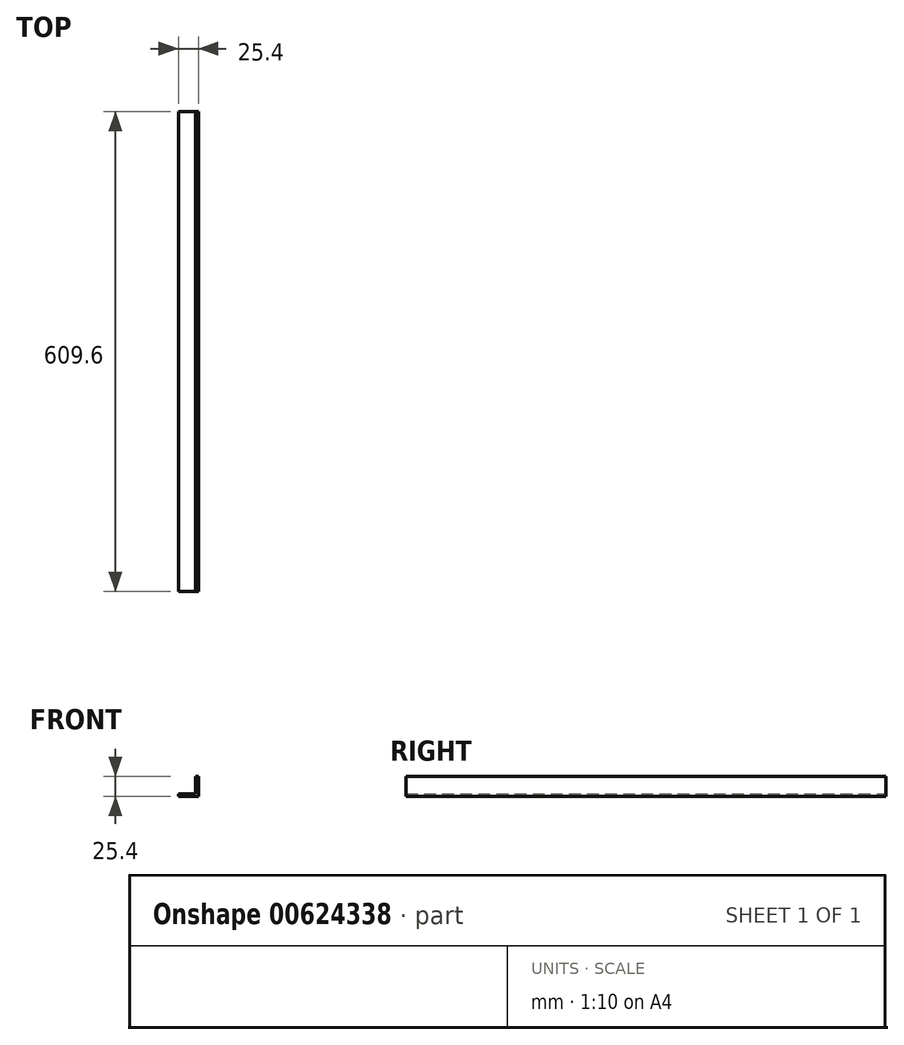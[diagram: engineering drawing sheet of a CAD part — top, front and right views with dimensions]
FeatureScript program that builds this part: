
annotation { "Feature Type Name" : "Feature", "Feature Type Description" : "" }
export const myFeature = defineFeature(function(context is Context, id is Id, definition is map)
    precondition{}
    {
        {
            var Q0;
            Q0=qCreatedBy(makeId("Front.planeOp"),FACE);
            var sketch = newSketch(context, id + "F0", { "sketchPlane" : qUnion([Q0])});
            skLineSegment(sketch, "E0", {"start": v(0, 0) * mm, "end": v(0, 25.4) * mm});
            skLineSegment(sketch, "E1", {"start": v(0, 25.4) * mm, "end": v(-3.25, 25.4) * mm});
            skLineSegment(sketch, "E2", {"start": v(-3.25, 25.4) * mm, "end": v(-3.25, 3.25) * mm});
            skLineSegment(sketch, "E3", {"start": v(-3.25, 3.25) * mm, "end": v(-25.4, 3.25) * mm});
            skLineSegment(sketch, "E4", {"start": v(-25.4, 3.25) * mm, "end": v(-25.4, 0) * mm});
            skLineSegment(sketch, "E5", {"start": v(-25.4, 0) * mm, "end": v(0, 0) * mm});
            skSolve(sketch);
        }
        {
            var Q0;
            Q0=makeQuery(id+"F0.imprint","IMPRINT",FACE,{"disambiguationData":[TD([[makeQuery(id+"F0.imprint","IMPRINT",EDGE,{"derivedFrom":sQuery(id+"F0.wireOp",EDGE,"E0")}),1.0]])]});
            extrude(context, id + "F1", {"entities" : qUnion([Q0]), "endBound" : BoundingType.SYMMETRIC, "depth" : 609.6 * mm, "offsetDistance" : 25.4 * mm});
        }
    });
